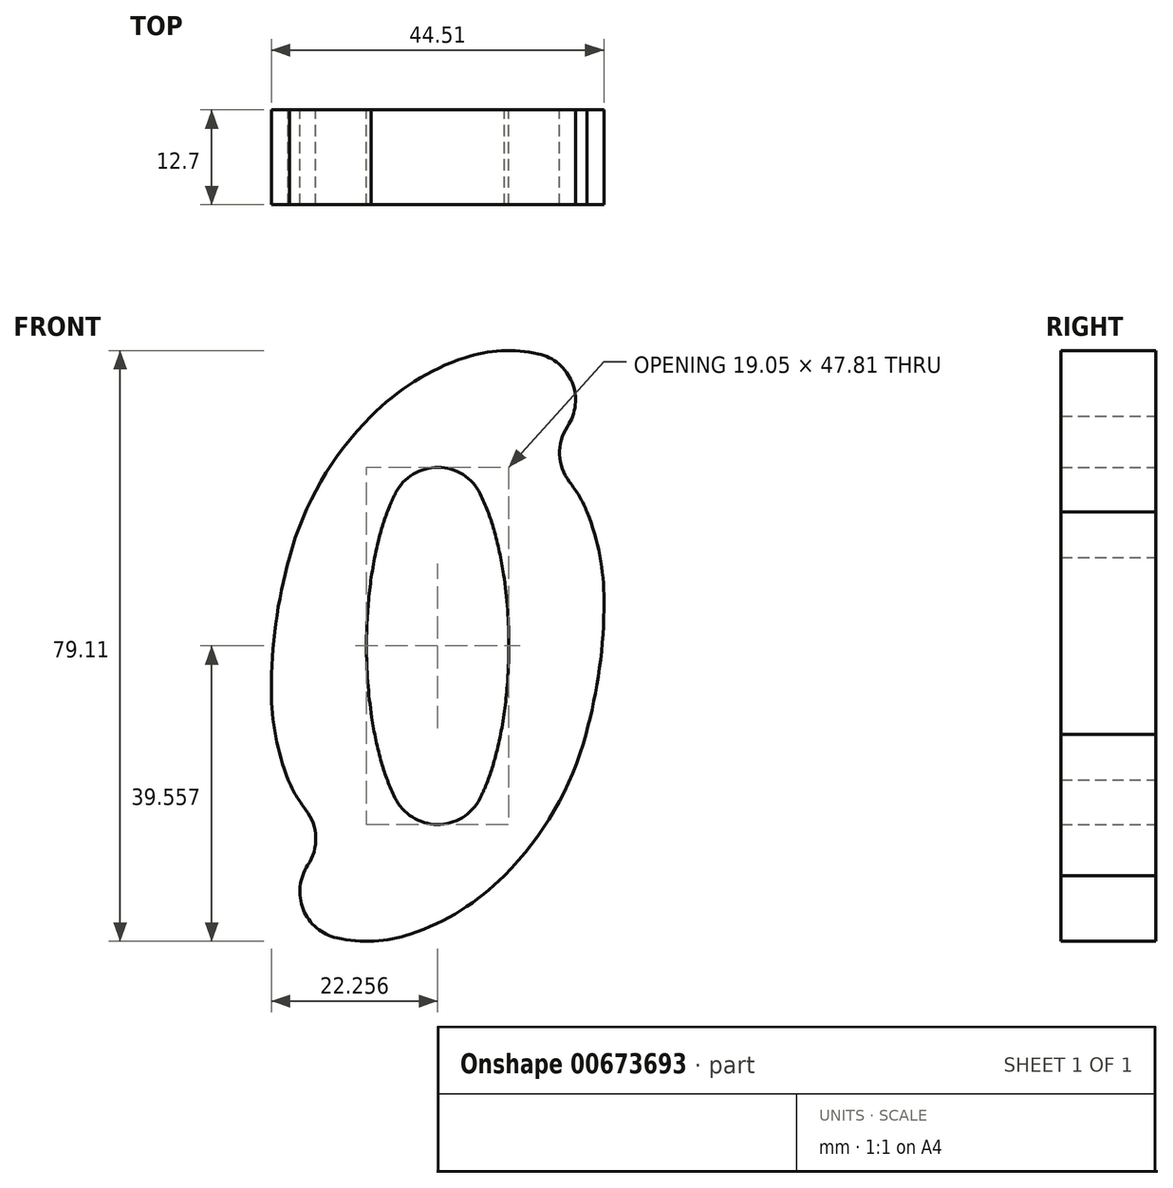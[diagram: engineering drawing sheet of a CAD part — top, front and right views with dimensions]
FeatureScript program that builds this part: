
annotation { "Feature Type Name" : "Feature", "Feature Type Description" : "" }
export const myFeature = defineFeature(function(context is Context, id is Id, definition is map)
    precondition{}
    {
        {
            var Q0;
            Q0=qCreatedBy(makeId("Front.planeOp"),FACE);
            var sketch = newSketch(context, id + "F0", { "sketchPlane" : qUnion([Q0])});
            skArc(sketch, "E0", {"start": v(316.68, 309.86) * mm, "mid": v(315.84, 307.52) * mm, "end": v(315.17, 305.12) * mm});
            skArc(sketch, "E1", {"start": v(315.17, 305.12) * mm, "mid": v(314.46, 301.68) * mm, "end": v(313.98, 298.2) * mm});
            skArc(sketch, "E2", {"start": v(313.98, 298.2) * mm, "mid": v(313.7, 294.7) * mm, "end": v(313.61, 291.17) * mm});
            skArc(sketch, "E3", {"start": v(313.61, 291.17) * mm, "mid": v(313.78, 286.38) * mm, "end": v(314.31, 281.61) * mm});
            skArc(sketch, "E4", {"start": v(314.31, 281.61) * mm, "mid": v(314.87, 278.56) * mm, "end": v(315.63, 275.55) * mm});
            skArc(sketch, "E5", {"start": v(315.63, 275.55) * mm, "mid": v(316.42, 273.16) * mm, "end": v(317.43, 270.85) * mm});
            skArc(sketch, "E6", {"start": v(317.43, 270.85) * mm, "mid": v(323.06, 267.28) * mm, "end": v(328.78, 270.73) * mm});
            skArc(sketch, "E7", {"start": v(328.78, 270.73) * mm, "mid": v(329.2, 271.61) * mm, "end": v(329.6, 272.52) * mm});
            skArc(sketch, "E8", {"start": v(329.6, 272.52) * mm, "mid": v(330.43, 274.86) * mm, "end": v(331.1, 277.25) * mm});
            skArc(sketch, "E9", {"start": v(331.1, 277.25) * mm, "mid": v(331.8, 280.69) * mm, "end": v(332.29, 284.16) * mm});
            skArc(sketch, "E10", {"start": v(332.29, 284.16) * mm, "mid": v(332.57, 287.68) * mm, "end": v(332.66, 291.2) * mm});
            skArc(sketch, "E11", {"start": v(332.66, 291.2) * mm, "mid": v(332.49, 296) * mm, "end": v(331.96, 300.76) * mm});
            skArc(sketch, "E12", {"start": v(331.96, 300.76) * mm, "mid": v(331.4, 303.81) * mm, "end": v(330.64, 306.82) * mm});
            skArc(sketch, "E13", {"start": v(330.64, 306.82) * mm, "mid": v(329.85, 309.21) * mm, "end": v(328.85, 311.52) * mm});
            skArc(sketch, "E14", {"start": v(328.85, 311.52) * mm, "mid": v(323.2, 315.09) * mm, "end": v(317.5, 311.65) * mm});
            skArc(sketch, "E15", {"start": v(317.5, 311.65) * mm, "mid": v(317.06, 310.76) * mm, "end": v(316.68, 309.86) * mm});
            skArc(sketch, "E16", {"start": v(300.88, 285.15) * mm, "mid": v(301.47, 294.16) * mm, "end": v(303.3, 303) * mm});
            skArc(sketch, "E17", {"start": v(303.3, 303) * mm, "mid": v(307.5, 313.2) * mm, "end": v(314.22, 321.93) * mm});
            skArc(sketch, "E18", {"start": v(314.22, 321.93) * mm, "mid": v(320.03, 326.6) * mm, "end": v(326.78, 329.78) * mm});
            skArc(sketch, "E19", {"start": v(326.78, 329.78) * mm, "mid": v(331.66, 330.72) * mm, "end": v(336.61, 330.3) * mm});
            skArc(sketch, "E20", {"start": v(336.61, 330.3) * mm, "mid": v(341.13, 326.46) * mm, "end": v(340.52, 320.57) * mm});
            skArc(sketch, "E21", {"start": v(340.52, 320.57) * mm, "mid": v(339.45, 316.8) * mm, "end": v(340.79, 313.14) * mm});
            skArc(sketch, "E22", {"start": v(340.79, 313.14) * mm, "mid": v(342.1, 311.2) * mm, "end": v(343.14, 309.1) * mm});
            skArc(sketch, "E23", {"start": v(343.14, 309.1) * mm, "mid": v(344.83, 303.27) * mm, "end": v(345.39, 297.24) * mm});
            skArc(sketch, "E24", {"start": v(345.39, 297.24) * mm, "mid": v(344.8, 288.22) * mm, "end": v(342.98, 279.37) * mm});
            skArc(sketch, "E25", {"start": v(342.98, 279.37) * mm, "mid": v(338.76, 269.18) * mm, "end": v(332.05, 260.44) * mm});
            skArc(sketch, "E26", {"start": v(332.05, 260.44) * mm, "mid": v(326.24, 255.77) * mm, "end": v(319.5, 252.6) * mm});
            skArc(sketch, "E27", {"start": v(319.5, 252.6) * mm, "mid": v(314.61, 251.66) * mm, "end": v(309.66, 252.08) * mm});
            skArc(sketch, "E28", {"start": v(309.66, 252.08) * mm, "mid": v(305.14, 255.9) * mm, "end": v(305.75, 261.8) * mm});
            skArc(sketch, "E29", {"start": v(305.75, 261.8) * mm, "mid": v(306.82, 265.56) * mm, "end": v(305.49, 269.23) * mm});
            skArc(sketch, "E30", {"start": v(305.49, 269.23) * mm, "mid": v(304.18, 271.16) * mm, "end": v(303.14, 273.25) * mm});
            skArc(sketch, "E31", {"start": v(303.14, 273.25) * mm, "mid": v(301.44, 279.1) * mm, "end": v(300.88, 285.15) * mm});
            skSolve(sketch);
        }
        {
            var Q0;
            Q0=makeQuery(id+"F0.imprint","IMPRINT",FACE,{"disambiguationData":[TD([[makeQuery(id+"F0.imprint","IMPRINT",EDGE,{"derivedFrom":sQuery(id+"F0.wireOp",EDGE,"E0")}),-1.0]])]});
            extrude(context, id + "F1", {"entities" : qUnion([Q0]), "depth" : 12.7 * mm, "offsetDistance" : 25.4 * mm});
        }
    });
